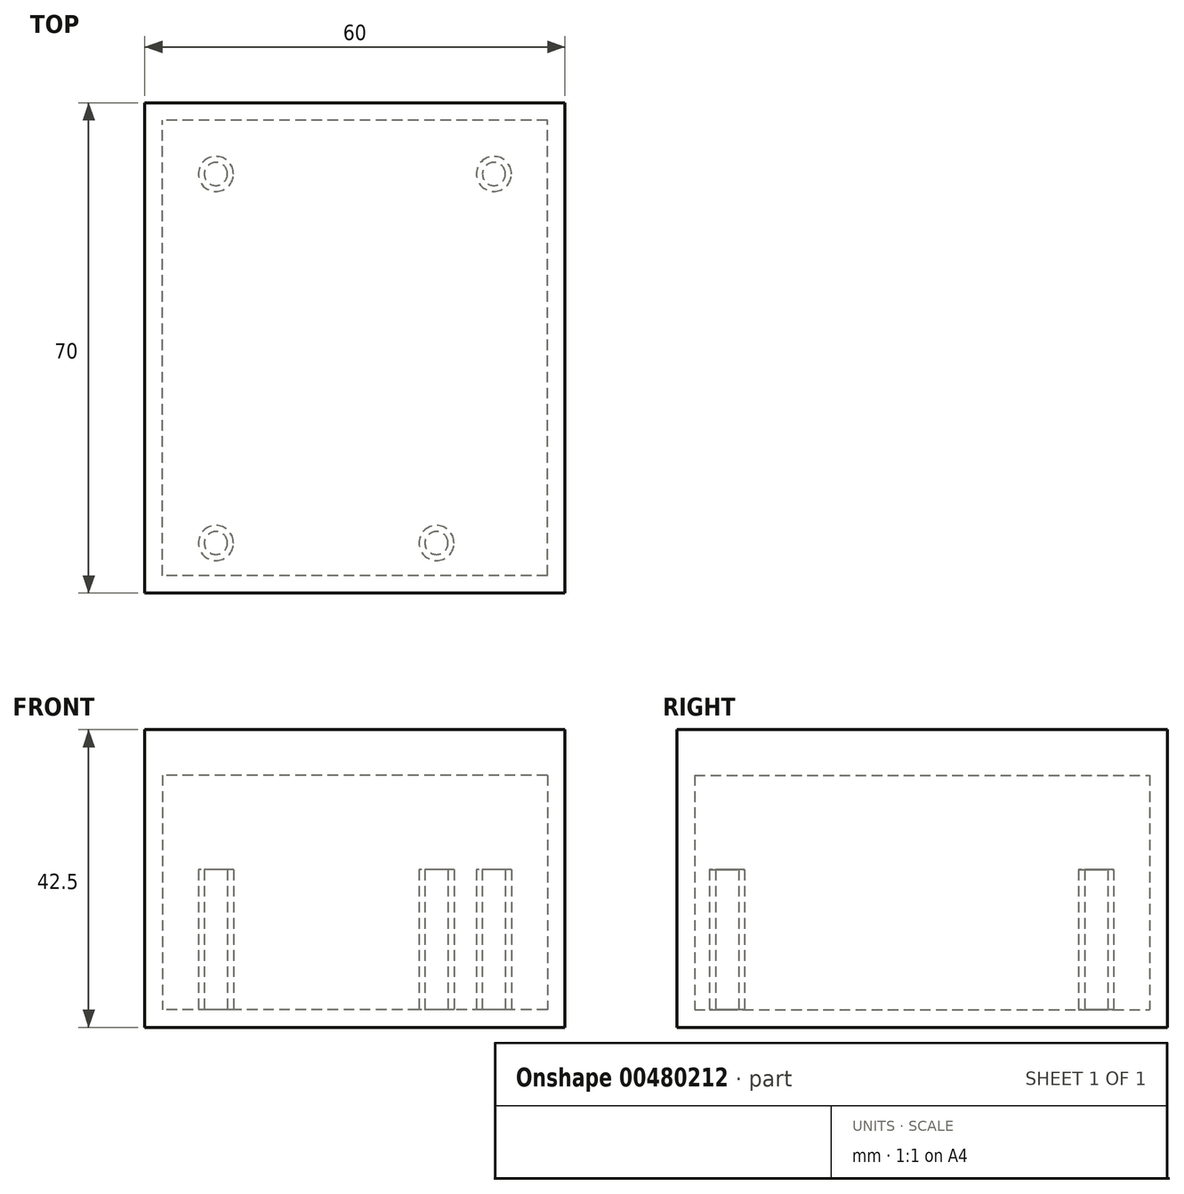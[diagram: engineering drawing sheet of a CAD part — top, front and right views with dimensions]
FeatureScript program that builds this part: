
annotation { "Feature Type Name" : "Feature", "Feature Type Description" : "" }
export const myFeature = defineFeature(function(context is Context, id is Id, definition is map)
    precondition{}
    {
        {
            assignVariable(context, id + "F0", {"name" : "hauteurboite", "anyValue" : 40});
        }
        {
            var Q0;
            Q0=qCreatedBy(makeId("Top.planeOp"),FACE);
            var sketch = newSketch(context, id + "F1", { "sketchPlane" : qUnion([Q0])});
            skLineSegment(sketch, "E0.bottom", {"start": v(30, -35) * mm, "end": v(-30, -35) * mm});
            skLineSegment(sketch, "E0.top", {"start": v(30, 35) * mm, "end": v(-30, 35) * mm});
            skLineSegment(sketch, "E0.left", {"start": v(30, -35) * mm, "end": v(30, 35) * mm});
            skLineSegment(sketch, "E0.right", {"start": v(-30, -35) * mm, "end": v(-30, 35) * mm});
            skPoint(sketch, "E0.middle", {"position": v(0, 0) * mm});
            skSolve(sketch);
        }
        {
            var Q0;
            Q0 = qSketchRegion(id + "F1", true);
            extrude(context, id + "F2", {"entities" : qUnion([Q0]), "depth" : (getVariable(context, 'hauteurboite')) * mm});
        }
        {
            var Q0;
            Q0=makeQuery(id+"F2.opExtrude","CAP_FACE",FACE,{"disambiguationData":[OSD([sQuery(id+"F1.wireOp",EDGE,"E0.bottom"),sQuery(id+"F1.wireOp",EDGE,"E0.top"),sQuery(id+"F1.wireOp",EDGE,"E0.left"),sQuery(id+"F1.wireOp",EDGE,"E0.right")])],"isStart":false});
            shell(context, id + "F3", {"entities" : qUnion([Q0]), "thickness" : 2.5 * mm});
        }
        {
            var Q0;
            Q0=makeQuery(id+"F2.opExtrude","CAP_FACE",FACE,{"disambiguationData":[OSD([sQuery(id+"F1.wireOp",EDGE,"E0.bottom"),sQuery(id+"F1.wireOp",EDGE,"E0.top"),sQuery(id+"F1.wireOp",EDGE,"E0.left"),sQuery(id+"F1.wireOp",EDGE,"E0.right")])],"isStart":false});
            var sketch = newSketch(context, id + "F4", { "sketchPlane" : qUnion([Q0])});
            skLineSegment(sketch, "E1.bottom", {"start": v(-27.5, 32.5) * mm, "end": v(27.5, 32.5) * mm});
            skLineSegment(sketch, "E1.top", {"start": v(-27.5, -32.5) * mm, "end": v(27.5, -32.5) * mm});
            skLineSegment(sketch, "E1.left", {"start": v(-27.5, 32.5) * mm, "end": v(-27.5, -32.5) * mm});
            skLineSegment(sketch, "E1.right", {"start": v(27.5, 32.5) * mm, "end": v(27.5, -32.5) * mm});
            skLineSegment(sketch, "E2.bottom", {"start": v(-30, 35) * mm, "end": v(30, 35) * mm});
            skLineSegment(sketch, "E2.top", {"start": v(-30, -35) * mm, "end": v(30, -35) * mm});
            skLineSegment(sketch, "E2.left", {"start": v(-30, 35) * mm, "end": v(-30, -35) * mm});
            skLineSegment(sketch, "E2.right", {"start": v(30, 35) * mm, "end": v(30, -35) * mm});
            skSolve(sketch);
        }
        {
            var Q0;
            Q0 = qSketchRegion(id + "F4", true);
            var Q1;
            Q1=makeQuery(id+"F4.imprint","IMPRINT",FACE,{"disambiguationData":[TD([[makeQuery(id+"F4.imprint","IMPRINT",EDGE,{"derivedFrom":sQuery(id+"F4.wireOp",EDGE,"E1.bottom")}),1.0]])]});
            extrude(context, id + "F5", {"entities" : qUnion([Q0, Q1]), "depth" : 2.5 * mm});
        }
        {
            var Q0;
            Q0=makeQuery(id+"F4.imprint","IMPRINT",FACE,{"disambiguationData":[TD([[makeQuery(id+"F4.imprint","IMPRINT",EDGE,{"derivedFrom":sQuery(id+"F4.wireOp",EDGE,"E1.bottom")}),1.0]])]});
            extrude(context, id + "F6", {"entities" : qUnion([Q0]), "operationType" : NewBodyOperationType.ADD, "oppositeDirection" : true, "depth" : 4 * mm});
        }
        {
            var Q0;
            Q0=makeQuery(id+"F3.opShell","OFFSET_FACE",FACE,{"disambiguationData":[OSD([sQuery(id+"F1.wireOp",EDGE,"E0.bottom"),sQuery(id+"F1.wireOp",EDGE,"E0.top"),sQuery(id+"F1.wireOp",EDGE,"E0.left"),sQuery(id+"F1.wireOp",EDGE,"E0.right")])]});
            var sketch = newSketch(context, id + "F7", { "sketchPlane" : qUnion([Q0])});
            skCircle(sketch, "E3", {"center": v(-19.85, 24.85) * mm, "radius": 1.65 * mm});
            skCircle(sketch, "E4.MirrorC", {"center": v(19.85, 24.85) * mm, "radius": 1.65 * mm});
            skCircle(sketch, "E5", {"center": v(-19.85, -27.85) * mm, "radius": 1.65 * mm});
            skCircle(sketch, "E6", {"center": v(11.65, -27.85) * mm, "radius": 1.65 * mm});
            skCircle(sketch, "E7", {"center": v(-19.85, 24.85) * mm, "radius": 2.5 * mm});
            skCircle(sketch, "E8.MirrorC", {"center": v(19.85, 24.85) * mm, "radius": 2.5 * mm});
            skCircle(sketch, "E9", {"center": v(-19.85, -27.85) * mm, "radius": 2.5 * mm});
            skCircle(sketch, "E10", {"center": v(11.65, -27.85) * mm, "radius": 2.5 * mm});
            skSolve(sketch);
        }
        {
            var Q0;
            Q0 = qSketchRegion(id + "F7", true);
            extrude(context, id + "F8", {"entities" : qUnion([Q0]), "operationType" : NewBodyOperationType.ADD, "depth" : 20 * mm});
        }
    });
